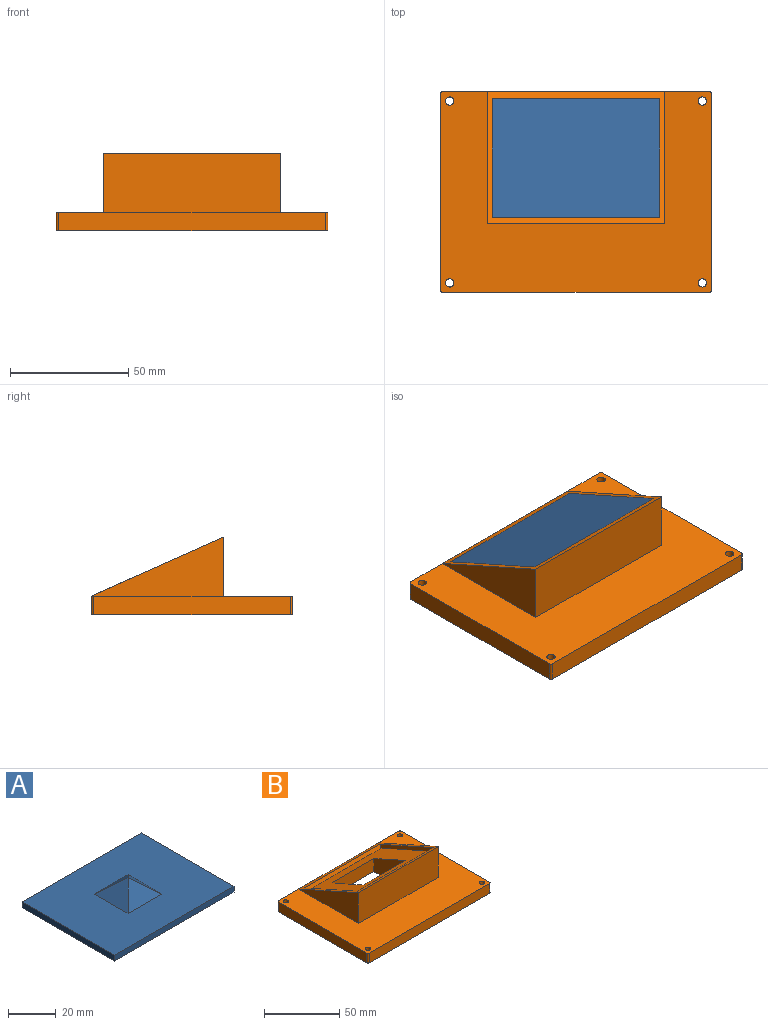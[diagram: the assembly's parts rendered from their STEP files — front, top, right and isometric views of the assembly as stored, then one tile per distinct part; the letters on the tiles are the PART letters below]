
ASSEMBLY  parts=2 mates=1
PART A: 10 faces, bbox 71x55x11.4 mm
  f0: plane 71x55mm, normal (0,0,1), area 3505mm2, adj f1,f2,f3,f4,f6,f7,f8,f9
  f1: plane 55x3mm, normal (-1,0,0), area 165mm2, adj f0,f2,f4,f5
  f2: plane 71x3mm, normal (0,-1,0), area 213mm2, adj f0,f1,f3,f5
  f3: plane 55x3mm, normal (1,0,0), area 165mm2, adj f0,f2,f4,f5
  f4: plane 71x3mm, normal (0,1,0), area 213mm2, adj f0,f1,f3,f5
  f5: plane 71x55mm, normal (0,0,-1), area 3905mm2, adj f1,f2,f3,f4
  f6: plane 20x10mm, normal (0,0.64,0.77), area 130.5mm2, adj f0,f7,f9
  f7: plane 20x10mm, normal (-0.64,0,0.77), area 130.5mm2, adj f0,f6,f8
  f8: plane 20x10mm, normal (0,-0.64,0.77), area 130.5mm2, adj f0,f7,f9
  f9: plane 20x10mm, normal (0.64,0,0.77), area 130.5mm2, adj f0,f6,f8
PART B: 61 faces, bbox 115x85x33 mm
  f0: plane 115x85mm, normal (0,0,-1), area 1177mm2, adj f1,f4,f5,f6,f7,f8,f9,f10
  f1: plane 113x8mm, normal (0,1,0), area 904mm2, adj f0,f3,f4,f14,f22
  f2: plane 105.19x75.19mm, normal (0,0,-1), area 6657.4mm2, adj f18,f19,f20,f21,f28,f29,f30,f31
  f3: plane 115x85mm, normal (0,0,1), area 5535.7mm2, adj f1,f4,f5,f6,f7,f8,f9,f10
  f4: cylinder r=1mm len=8mm, axis (0,0,-1), area 12.6mm2, adj f0,f1,f3,f5
  f5: plane 83x8mm, normal (-1,0,0), area 664mm2, adj f0,f3,f4,f6
  f6: cylinder r=1mm len=8mm, axis (0,0,-1), area 12.6mm2, adj f0,f3,f5,f7
  f7: plane 113x8mm, normal (0,-1,0), area 904mm2, adj f0,f3,f6,f8
  f8: cylinder r=1mm len=8mm, axis (0,0,-1), area 12.6mm2, adj f0,f3,f7,f9
  f9: plane 83x8mm, normal (1,0,0), area 664mm2, adj f0,f3,f8,f14
  f10: cylinder r=1.75mm len=8mm, axis (0,0,-1), area 88mm2, adj f0,f3
  f11: cylinder r=1.75mm len=8mm, axis (0,0,-1), area 88mm2, adj f0,f3
  f12: cylinder r=1.75mm len=8mm, axis (0,0,-1), area 88mm2, adj f0,f3
  f13: cylinder r=1.75mm len=8mm, axis (0,0,-1), area 88mm2, adj f0,f3
  f14: cylinder r=1mm len=8mm, axis (0,0,-1), area 12.6mm2, adj f0,f1,f3,f9
  f15: plane 56x25mm, normal (1,0,0), area 700mm2, adj f3,f17,f22
  f16: plane 56x25mm, normal (-1,0,0), area 700mm2, adj f3,f17,f22
  f17: plane 75x25mm, normal (0,-1,0), area 1875mm2, adj f3,f15,f16,f22
  f18: plane 40x23.91mm, normal (0,1,0), area 956.4mm2, adj f2,f19,f21,f27
  f19: plane 30x23.91mm, normal (1,0,0), area 516.4mm2, adj f2,f18,f20,f27
  f20: plane 40x10.52mm, normal (0,-1,0), area 420.7mm2, adj f2,f19,f21,f27
  f21: plane 30x23.91mm, normal (-1,0,0), area 516.4mm2, adj f2,f18,f20,f27
  f22: plane 75x56mm, normal (0,0.41,0.91), area 694.5mm2, adj f1,f15,f16,f17,f23,f24,f25,f26
  f23: plane 51.45x25.16mm, normal (1,0,0), area 165mm2, adj f22,f24,f26,f27
  f24: plane 71x2.74mm, normal (0,-0.91,0.41), area 213mm2, adj f22,f23,f25,f27
  f25: plane 51.45x25.16mm, normal (-1,0,0), area 165mm2, adj f22,f24,f26,f27
  f26: plane 71x2.74mm, normal (0,0.91,-0.41), area 213mm2, adj f22,f23,f25,f27
  f27: plane 71x50.22mm, normal (0,0.41,0.91), area 2590.9mm2, adj f18,f19,f20,f21,f23,f24,f25,f26
  f28: cylinder r=3mm len=2.62mm, axis (0,0,-1), area 4.8mm2, adj f2,f29,f59,f60
  f29: cylinder r=5.05mm len=1.97mm, axis (0,0,-1), area 4.2mm2, adj f2,f28,f30,f60
  f30: cylinder r=3mm len=2.79mm, axis (0,0,-1), area 5mm2, adj f2,f29,f31,f60
  f31: plane 92.81x1.5mm, normal (0,-1,0), area 139.2mm2, adj f2,f30,f32,f60
  f32: cylinder r=3mm len=2.62mm, axis (0,0,-1), area 4.8mm2, adj f2,f31,f33,f60
  f33: cylinder r=5mm len=1.92mm, axis (0,0,-1), area 4.1mm2, adj f2,f32,f34,f60
  f34: cylinder r=3mm len=2.62mm, axis (0,0,-1), area 4.8mm2, adj f2,f33,f35,f60
  f35: plane 62.98x1.5mm, normal (-1,0,0), area 94.5mm2, adj f2,f34,f36,f60
  f36: cylinder r=3mm len=2.62mm, axis (0,0,-1), area 4.8mm2, adj f2,f35,f37,f60
  f37: cylinder r=5.05mm len=1.97mm, axis (0,0,-1), area 4.2mm2, adj f2,f36,f38,f60
  f38: cylinder r=3mm len=2.62mm, axis (0,0,-1), area 4.8mm2, adj f2,f37,f39,f60
  f39: plane 92.92x1.5mm, normal (0,1,0), area 139.4mm2, adj f2,f38,f40,f60
  f40: cylinder r=3mm len=2.62mm, axis (0,0,-1), area 4.8mm2, adj f2,f39,f41,f60
  f41: cylinder r=5.05mm len=1.97mm, axis (0,0,-1), area 4.2mm2, adj f2,f40,f42,f60
  f42: cylinder r=3mm len=2.62mm, axis (0,0,-1), area 4.8mm2, adj f2,f41,f59,f60
  f43: cylinder r=3.05mm len=1.9mm, axis (0,0,-1), area 4.2mm2, adj f0,f44,f58,f60
  f44: cylinder r=3mm len=2.84mm, axis (0,0,-1), area 5.6mm2, adj f0,f43,f45,f60
  f45: plane 65.54x1.5mm, normal (-1,0,0), area 98.3mm2, adj f0,f44,f46,f60
  f46: cylinder r=3mm len=2.84mm, axis (0,0,-1), area 5.6mm2, adj f0,f45,f47,f60
  f47: cylinder r=3.05mm len=1.91mm, axis (0,0,-1), area 4.2mm2, adj f0,f46,f48,f60
  f48: cylinder r=3mm len=2.84mm, axis (0,0,-1), area 5.6mm2, adj f0,f47,f49,f60
  f49: plane 95.54x1.5mm, normal (0,-1,0), area 143.3mm2, adj f0,f48,f50,f60
  f50: cylinder r=3mm len=2.84mm, axis (0,0,-1), area 5.6mm2, adj f0,f49,f51,f60
  f51: cylinder r=3.05mm len=1.91mm, axis (0,0,-1), area 4.2mm2, adj f0,f50,f52,f60
  f52: cylinder r=3mm len=2.84mm, axis (0,0,-1), area 5.6mm2, adj f0,f51,f53,f60
  f53: plane 65.54x1.5mm, normal (1,0,0), area 98.3mm2, adj f0,f52,f54,f60
  f54: cylinder r=3mm len=2.84mm, axis (0,0,-1), area 5.6mm2, adj f0,f53,f55,f60
  f55: cylinder r=3.05mm len=1.9mm, axis (0,0,-1), area 4.2mm2, adj f0,f54,f56,f60
  f56: cylinder r=3mm len=2.83mm, axis (0,0,-1), area 5.6mm2, adj f0,f55,f57,f60
  f57: plane 95.58x1.5mm, normal (0,1,0), area 143.4mm2, adj f0,f56,f58,f60
  f58: cylinder r=3mm len=2.83mm, axis (0,0,-1), area 5.6mm2, adj f0,f43,f57,f60
  f59: plane 62.92x1.5mm, normal (1,0,0), area 94.4mm2, adj f2,f28,f42,f60
  f60: plane 109.13x79.06mm, normal (0,0,-1), area 701.4mm2, adj f28,f29,f30,f31,f32,f33,f34,f35
PLACE A rot(axis=(1,0,0),155.9deg) t=(3.11,5.57,13.76)mm
PLACE B t=(-3.33,-5.35,-9.45)mm
MATE parallel B.f22 <-> A.f5  axis (0,0.41,0.91) through (1.09,-16.35,23.55)mm
